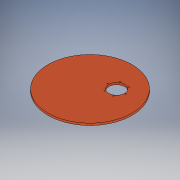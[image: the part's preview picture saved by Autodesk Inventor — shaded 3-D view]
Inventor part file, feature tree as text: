
AUTODESK INVENTOR PART (.ipt)
format: ipt  version: 2018 (Build 220112000, 112)  size: 125,440 bytes
history: native  units: in
note: dims shown in document units (in); Inventor stores cm internally (conversion verified against a paired STEP export)
features: sketch x3, extrude x2, hole x1
ambient origin geometry x8: Origin, YZ Plane, XZ Plane, XY Plane, X Axis, Y Axis, Z Axis, Center Point
bodies: Solid1 (feature_tree)
feature tree (6):
  extrude  "Extrusion1"  Depth=0.375in TaperAngle=0.0deg
  hole  "Hole1"  [1 undecoded]
  extrude  "Extrusion2"  TaperAngle=0.0deg  [1 undecoded]
  sketch  "Sketch1"  dims[d0=16.0in d1=0.375in d2=0.0in]
  sketch  "Sketch2"  dims[d3=3.6in d4=45.0deg]
  sketch  "Sketch3"  dims[d5=1.7in d6=0.0in d7=2.3622in d9=360.0deg d11=0.163in d12=0.394in d13=0.375in d14=0.25in d15=0.5635in d16=0.559in d17=0.8108in d18=3.6in d19=45.0deg d20=3.0in d21=0.375in d22=0.0in]
note: 2 required parameter values undecoded (feature->parameter linkage not recoverable at this tier; creation-order binding heuristic only, values carry confidence <= 0.55)
